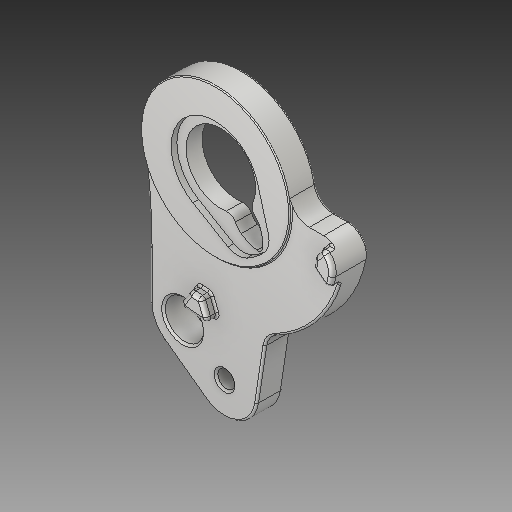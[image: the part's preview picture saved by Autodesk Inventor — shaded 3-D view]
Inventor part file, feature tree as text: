
AUTODESK INVENTOR PART (.ipt)
format: ipt  version: 2019 (Build 230136000, 136)  size: 423,424 bytes
history: native  units: in
note: dims shown in document units (in); Inventor stores cm internally (conversion verified against a paired STEP export)
features: sketch x8, other x5, plane x2
ambient origin geometry x8: Origin, YZ Plane, XZ Plane, XY Plane, X Axis, Y Axis, Z Axis, Center Point
bodies: Solid1 (feature_tree)
feature tree (15):
  other  "Rear Pivot Lock Plate.ipt"
  other  "Solid1::Rear Pivot Lock Plate.ipt"
  other  "TaggingFeature1"
  sketch  "Sketch1"  dims[d0=0.3937in]
  sketch  "Sketch2"
  sketch  "Sketch3"
  sketch  "Sketch4"
  sketch  "Sketch5"
  sketch  "Sketch6"
  sketch  "Sketch7"
  sketch  "Sketch8"
  plane  "Work Plane1"
  plane  "Work Plane2"
  other  "Work Axis1"
  other  "Work Axis2"
